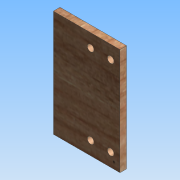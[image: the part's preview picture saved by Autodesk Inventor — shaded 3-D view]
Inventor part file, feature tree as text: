
AUTODESK INVENTOR PART (.ipt)
format: ipt  version: 2015 (Build 190159000, 159)  size: 182,272 bytes
history: native  units: mm
features: other x5, extrude x2, sketch x2, projected_geometry x1
ambient origin geometry x8: Origin, YZ Plane, XZ Plane, XY Plane, X Axis, Y Axis, Z Axis, Center Point
bodies: Body1 (feature_tree)
feature tree (10):
  other  "Blocks"
  extrude  "Extrusion12"  Depth=5.0mm
  extrude  "Extrusion13"  Depth=5.0mm
  other  "Block1"
  other  "Block2"
  other  "Block3"
  other  "Block4"
  sketch  "Sketch45"  dims[d197=5.0mm d199=5.0mm]
  sketch  "Sketch46"  dims[d200=5.0mm d201=60.0mm d202=80.0mm d203=10.0mm d204=10.0mm d205=15.0mm d206=30.0mm d207=8.0mm d210=5.0mm d211=5.0mm d212=0.0mm d213=20.0mm d214=5.0mm d215=0.0mm d29=1.0mm d30=1.0mm]
  projected_geometry  "Projected Loop4"
